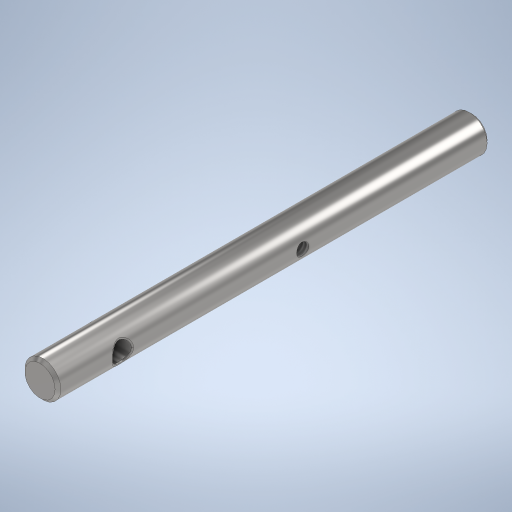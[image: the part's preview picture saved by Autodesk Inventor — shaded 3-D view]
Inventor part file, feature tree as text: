
AUTODESK INVENTOR PART (.ipt)
format: ipt  version: 2023 (Build 270158000, 158)  size: 318,464 bytes
history: native  units: in
note: dims shown in document units (in); Inventor stores cm internally (conversion verified against a paired STEP export)
features: sketch x3, hole x2, extrude x1, chamfer x1, plane x1, fillet x1
ambient origin geometry x8: Origin, YZ Plane, XZ Plane, XY Plane, X Axis, Y Axis, Z Axis, Center Point
bodies: Solid1 (feature_tree)
feature tree (9):
  extrude  "Extrusion1"  Depth=3.0in TaperAngle=0.0deg
  chamfer  "Chamfer1"  Distance=0.02in Angle=45.0deg
  plane  "Work Plane1"
  hole  "Hole1"  [1 undecoded]
  fillet  "Fillet1"  Radius=0.204in
  hole  "Hole2"  [1 undecoded]
  sketch  "Sketch1"  dims[d0=0.25in d1=3.0in d2=0.0in d3=0.02in d4=0.125in d5=45.0deg]
  sketch  "Sketch2"  dims[d6=0.125in d7=0.45in d8=0.204in]
  sketch  "Sketch3"  dims[d9=0.1339in d10=0.75in d11=0.256in d12=0.118in d13=90.0deg d14=1.0in d15=0.8108in d16=0.0079in d17=1.7in d18=0.0849in d19=0.1in d20=0.375in d21=0.25in d22=0.5635in d23=0.125in d24=0.8108in]
note: 2 required parameter values undecoded (feature->parameter linkage not recoverable at this tier; creation-order binding heuristic only, values carry confidence <= 0.55)
